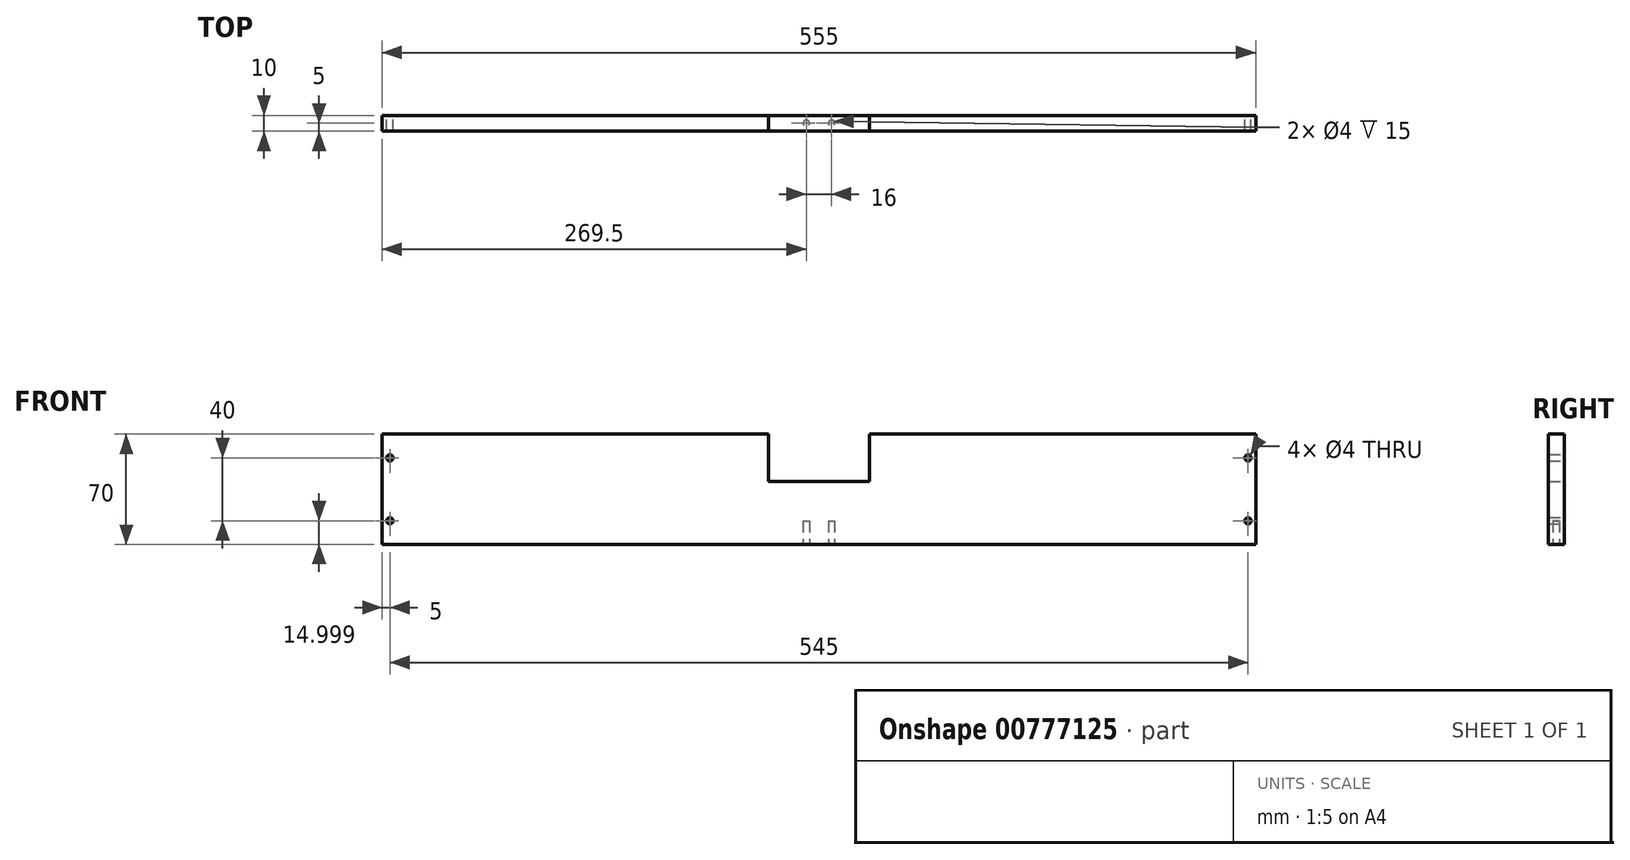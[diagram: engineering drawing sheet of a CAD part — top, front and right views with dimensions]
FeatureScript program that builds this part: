
annotation { "Feature Type Name" : "Feature", "Feature Type Description" : "" }
export const myFeature = defineFeature(function(context is Context, id is Id, definition is map)
    precondition{}
    {
        {
            var Q0;
            Q0=qCreatedBy(makeId("Front.planeOp"),FACE);
            var sketch = newSketch(context, id + "F0", { "sketchPlane" : qUnion([Q0])});
            skLineSegment(sketch, "E0.bottom", {"start": v(-277.5, 68.6) * mm, "end": v(277.5, 68.6) * mm});
            skLineSegment(sketch, "E0.top", {"start": v(-277.5, -1.4) * mm, "end": v(277.5, -1.4) * mm});
            skLineSegment(sketch, "E0.left", {"start": v(-277.5, 68.6) * mm, "end": v(-277.5, -1.4) * mm});
            skLineSegment(sketch, "E0.right", {"start": v(277.5, 68.6) * mm, "end": v(277.5, -1.4) * mm});
            skCircle(sketch, "E1", {"center": v(-272.5, 13.6) * mm, "radius": 2 * mm});
            skCircle(sketch, "E2", {"center": v(-272.5, 53.6) * mm, "radius": 2 * mm});
            skCircle(sketch, "E3", {"center": v(272.5, 13.6) * mm, "radius": 2 * mm});
            skCircle(sketch, "E4", {"center": v(272.5, 53.6) * mm, "radius": 2 * mm});
            skLineSegment(sketch, "E5.bottom", {"start": v(0, 68.6) * mm, "end": v(32, 68.6) * mm});
            skLineSegment(sketch, "E5.top", {"start": v(0, 38.6) * mm, "end": v(32, 38.6) * mm});
            skLineSegment(sketch, "E5.left", {"start": v(0, 68.6) * mm, "end": v(0, 38.6) * mm});
            skLineSegment(sketch, "E5.right", {"start": v(32, 68.6) * mm, "end": v(32, 38.6) * mm});
            skLineSegment(sketch, "E6.bottom", {"start": v(0, 38.6) * mm, "end": v(-32, 38.6) * mm});
            skLineSegment(sketch, "E6.top", {"start": v(0, 68.6) * mm, "end": v(-32, 68.6) * mm});
            skLineSegment(sketch, "E6.left", {"start": v(0, 38.6) * mm, "end": v(0, 68.6) * mm});
            skLineSegment(sketch, "E6.right", {"start": v(-32, 38.6) * mm, "end": v(-32, 68.6) * mm});
            skSolve(sketch);
        }
        {
            var Q0;
            Q0=makeQuery(id+"F0.imprint","IMPRINT",FACE,{"disambiguationData":[TD([[makeQuery(id+"F0.imprint","IMPRINT",EDGE,{"derivedFrom":sQuery(id+"F0.wireOp",EDGE,"E0.top")}),1.0]])]});
            extrude(context, id + "F1", {"entities" : qUnion([Q0]), "depth" : 10 * mm, "offsetDistance" : 25 * mm});
        }
        {
            var Q0;
            Q0=makeQuery(id+"F1.opExtrude","SWEPT_FACE",FACE,{"disambiguationData":[OSD([sQuery(id+"F0.wireOp",EDGE,"E0.top")])]});
            var sketch = newSketch(context, id + "F2", { "sketchPlane" : qUnion([Q0])});
            skCircle(sketch, "E7", {"center": v(-8, 5) * mm, "radius": 2 * mm});
            skCircle(sketch, "E8", {"center": v(8, 5) * mm, "radius": 2 * mm});
            skSolve(sketch);
        }
        {
            var Q0;
            Q0=makeQuery(id+"F2.imprint","IMPRINT",FACE,{"disambiguationData":[TD([[makeQuery(id+"F2.imprint","IMPRINT",EDGE,{"derivedFrom":sQuery(id+"F2.wireOp",EDGE,"E7")}),1.0]])]});
            var Q1;
            Q1=makeQuery(id+"F2.imprint","IMPRINT",FACE,{"disambiguationData":[TD([[makeQuery(id+"F2.imprint","IMPRINT",EDGE,{"derivedFrom":sQuery(id+"F2.wireOp",EDGE,"E8")}),1.0]])]});
            extrude(context, id + "F3", {"entities" : qUnion([Q0, Q1]), "operationType" : NewBodyOperationType.REMOVE, "oppositeDirection" : true, "depth" : 15 * mm, "offsetDistance" : 25 * mm});
        }
    });
